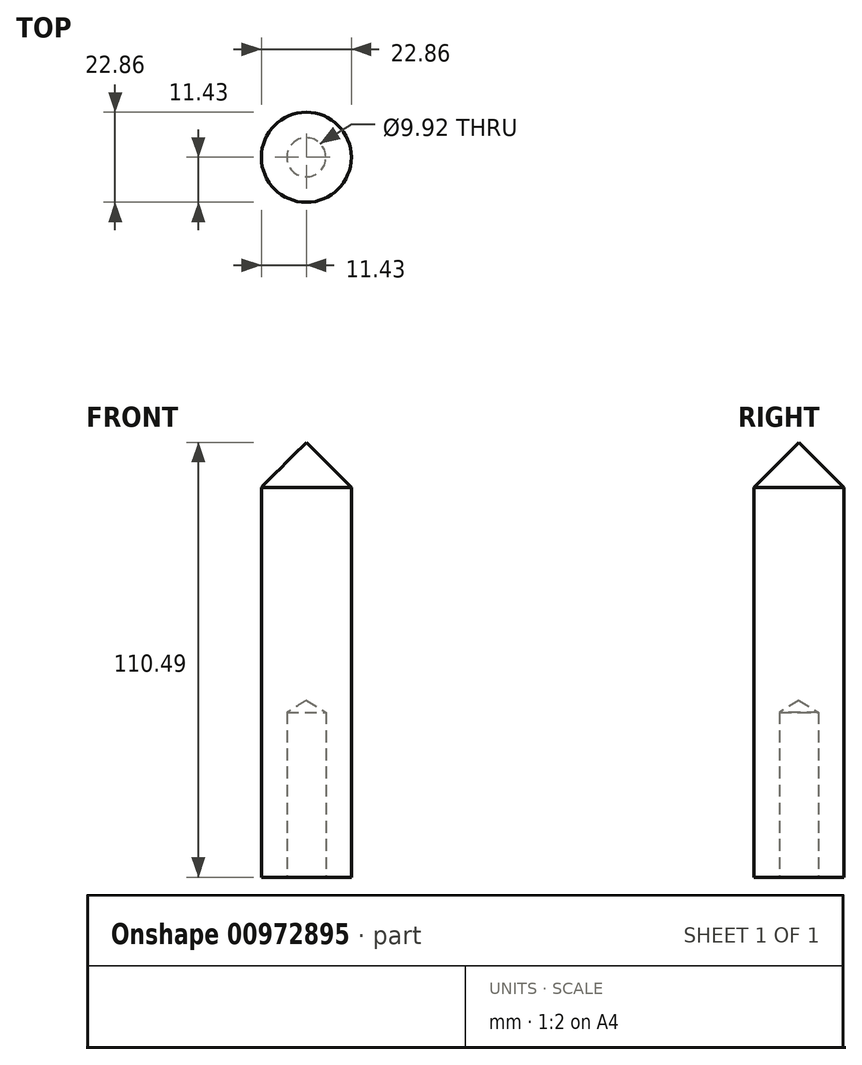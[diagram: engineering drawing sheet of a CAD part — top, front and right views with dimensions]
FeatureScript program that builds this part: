
annotation { "Feature Type Name" : "Feature", "Feature Type Description" : "" }
export const myFeature = defineFeature(function(context is Context, id is Id, definition is map)
    precondition{}
    {
        {
            var Q0;
            Q0=qCreatedBy(makeId("Front.planeOp"),FACE);
            var sketch = newSketch(context, id + "F0", { "sketchPlane" : qUnion([Q0])});
            skLineSegment(sketch, "E0", {"start": v(0, 0) * mm, "end": v(0, 11.43) * mm});
            skLineSegment(sketch, "E1", {"start": v(0, 0) * mm, "end": v(11.43, 0) * mm});
            skLineSegment(sketch, "E2", {"start": v(11.43, 0) * mm, "end": v(0, 11.43) * mm});
            skSolve(sketch);
        }
        {
            var Q0;
            Q0=makeQuery(id+"F0.imprint","IMPRINT",FACE,{"disambiguationData":[TD([[makeQuery(id+"F0.imprint","IMPRINT",EDGE,{"derivedFrom":sQuery(id+"F0.wireOp",EDGE,"E0")}),-1.0]])]});
            var Q1;
            Q1=sQuery(id+"F0.wireOp",EDGE,"E0");
            revolve(context, id + "F1", {"surfaceOperationType" : NewSurfaceOperationType.NEW, "entities" : qUnion([Q0]), "axis" : qUnion([Q1]), "revolveType" : RevolveType.FULL});
        }
        {
            var Q0;
            Q0=makeQuery(id+"F1.opRevolve","SWEPT_FACE",FACE,{"disambiguationData":[OSD([sQuery(id+"F0.wireOp",EDGE,"E1")])]});
            extrude(context, id + "F2", {"entities" : qUnion([Q0]), "operationType" : NewBodyOperationType.ADD, "depth" : 99.06 * mm, "offsetDistance" : 25.4 * mm});
        }
        {
            var Q0;
            Q0=makeQuery(id+"F2.opExtrude","CAP_FACE",FACE,{"disambiguationData":[OSD([sQuery(id+"F0.wireOp",EDGE,"E1")])],"isStart":false});
            var sketch = newSketch(context, id + "F3", { "sketchPlane" : qUnion([Q0])});
            skLineSegment(sketch, "E3", {"start": v(0, -11.43) * mm, "end": v(0, 0) * mm});
            skLineSegment(sketch, "E4", {"start": v(0, 0) * mm, "end": v(-11.43, 0) * mm});
            skSolve(sketch);
        }
        {
            var Q0;
            Q0=sQuery(id+"F3.wireOp",VERTEX,"E3.end");
            var Q1;
            Q1=makeQuery(id+"F1.opRevolve","SWEPT_BODY",BODY,{"disambiguationData":[OSD([sQuery(id+"F0.wireOp",EDGE,"E0"),sQuery(id+"F0.wireOp",EDGE,"E1"),sQuery(id+"F0.wireOp",EDGE,"E2")])]});
            hole(context, id + "F4", {"style" : HoleStyle.SIMPLE, "endStyle" : HoleEndStyle.BLIND, "standardTappedOrClearance" : lookupTablePath({ "standard" : "ANSI", "engagement" : "75%", "pitch" : "20 tpi", "size" : "7/16", "type" : "Tapped" }), "standardBlindInLast" : lookupTablePath({ "standard" : "ANSI", "fit" : "Normal", "engagement" : "75%", "pitch" : "20 tpi", "size" : "7/16", "type" : "Clearance & tapped" }), "holeDiameter" : 9.92 * mm, "majorDiameter" : 11.1 * mm, "showTappedDepth" : true, "holeDepth" : 41.9 * mm, "isTappedThrough" : true, "tappedDepth" : 38.1 * mm, "tapClearance" : 3, "locations" : qUnion([Q0]), "scope" : qUnion([Q1])});
        }
    });
